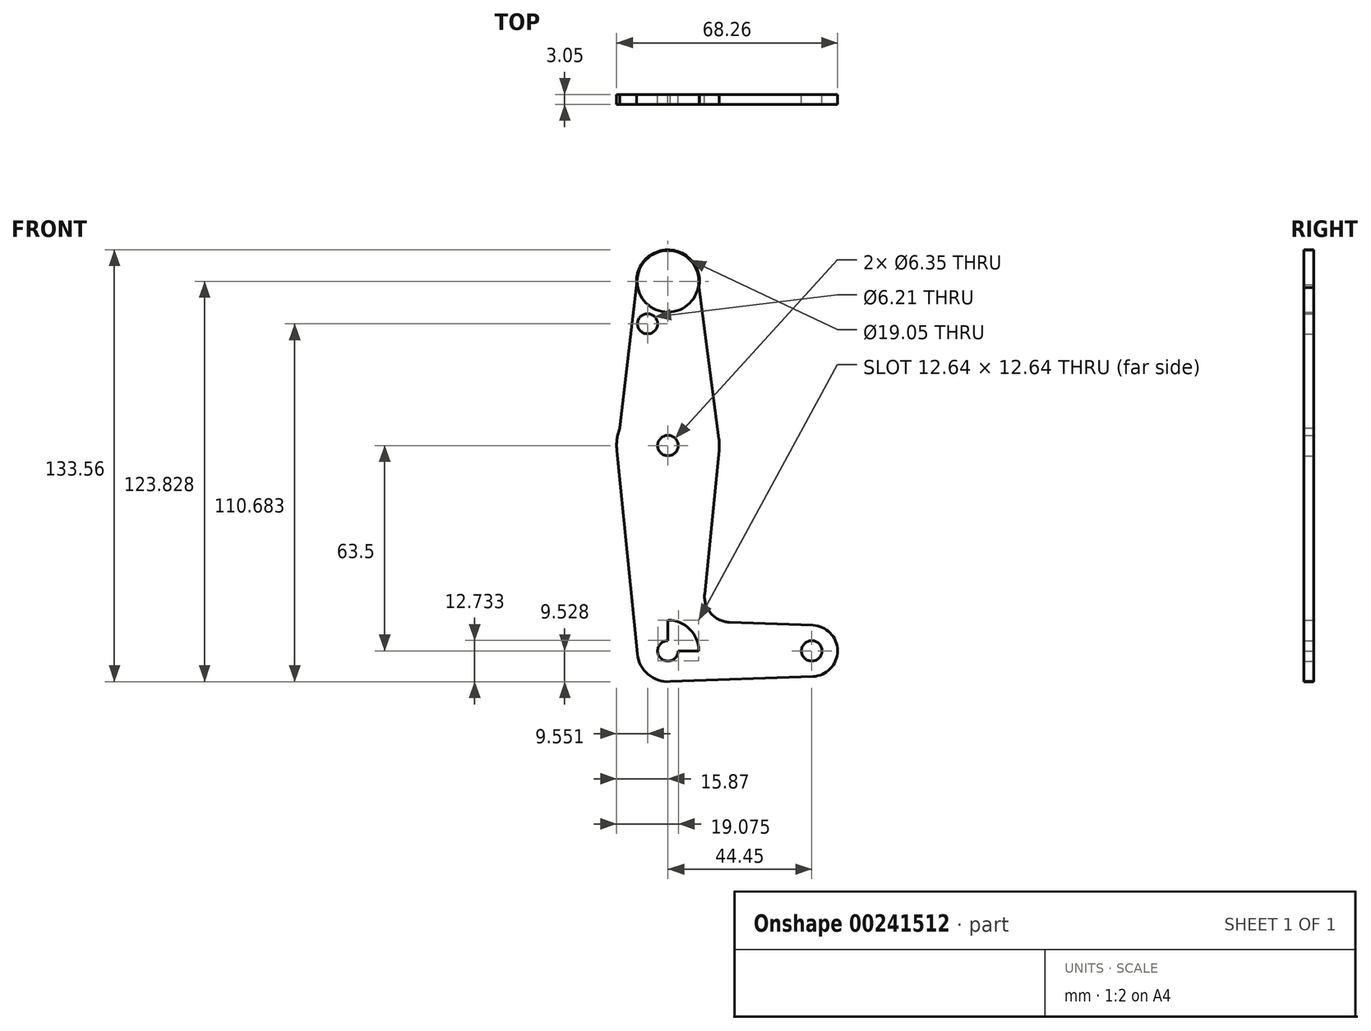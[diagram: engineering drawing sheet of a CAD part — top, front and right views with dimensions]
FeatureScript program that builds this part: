
annotation { "Feature Type Name" : "Feature", "Feature Type Description" : "" }
export const myFeature = defineFeature(function(context is Context, id is Id, definition is map)
    precondition{}
    {
        {
            var Q0;
            Q0=qCreatedBy(makeId("Front.planeOp"),FACE);
            var sketch = newSketch(context, id + "F0", { "sketchPlane" : qUnion([Q0])});
            skCircle(sketch, "E0", {"center": v(0, 67.53) * mm, "radius": 9.73 * mm});
            skCircle(sketch, "E1", {"center": v(0, 67.53) * mm, "radius": 9.53 * mm});
            skLineSegment(sketch, "E2", {"start": v(0, 67.53) * mm, "end": v(0, -46.77) * mm});
            skLineSegment(sketch, "E3", {"start": v(0, -46.77) * mm, "end": v(44.45, -46.77) * mm});
            skCircle(sketch, "E4", {"center": v(0, 16.73) * mm, "radius": 15.88 * mm});
            skCircle(sketch, "E5", {"center": v(0, -46.77) * mm, "radius": 9.53 * mm});
            skCircle(sketch, "E6", {"center": v(44.45, -46.77) * mm, "radius": 7.94 * mm});
            skLineSegment(sketch, "E7", {"start": v(0, 16.73) * mm, "end": v(0, -46.77) * mm});
            skLineSegment(sketch, "E8", {"start": v(-9.52, 67.76) * mm, "end": v(-15.78, 15.02) * mm});
            skLineSegment(sketch, "E9", {"start": v(-15.78, 15.02) * mm, "end": v(-9.48, -47.72) * mm});
            skLineSegment(sketch, "E10", {"start": v(9.45, 66.33) * mm, "end": v(16.24, 15.02) * mm});
            skLineSegment(sketch, "E11", {"start": v(15.8, 15.14) * mm, "end": v(11.34, -29.18) * mm});
            skLineSegment(sketch, "E12", {"start": v(18.97, -37.92) * mm, "end": v(44.73, -38.84) * mm});
            skLineSegment(sketch, "E13", {"start": v(0, -56.3) * mm, "end": v(44.73, -54.7) * mm});
            skCircle(sketch, "E14", {"center": v(0, 67.53) * mm, "radius": 3.18 * mm});
            skCircle(sketch, "E15", {"center": v(0, 16.73) * mm, "radius": 3.18 * mm});
            skCircle(sketch, "E16", {"center": v(0, -46.77) * mm, "radius": 3.18 * mm});
            skCircle(sketch, "E17", {"center": v(44.45, -46.77) * mm, "radius": 3.18 * mm});
            skPoint(sketch, "E18.newPointA", {"position": v(9.48, -47.72) * mm});
            skArc(sketch, "E18.filletArc", {"start": v(11.34, -29.18) * mm, "mid": v(13.26, -35.2) * mm, "end": v(18.97, -37.92) * mm});
            skCircle(sketch, "E19", {"center": v(-6.32, 54.38) * mm, "radius": 3.1 * mm});
            skSolve(sketch);
        }
        {
            var Q0;
            Q0 = qSketchRegion(id + "F0", true);
            extrude(context, id + "F1", {"entities" : qUnion([Q0]), "depth" : 3.05 * mm});
        }
    });
